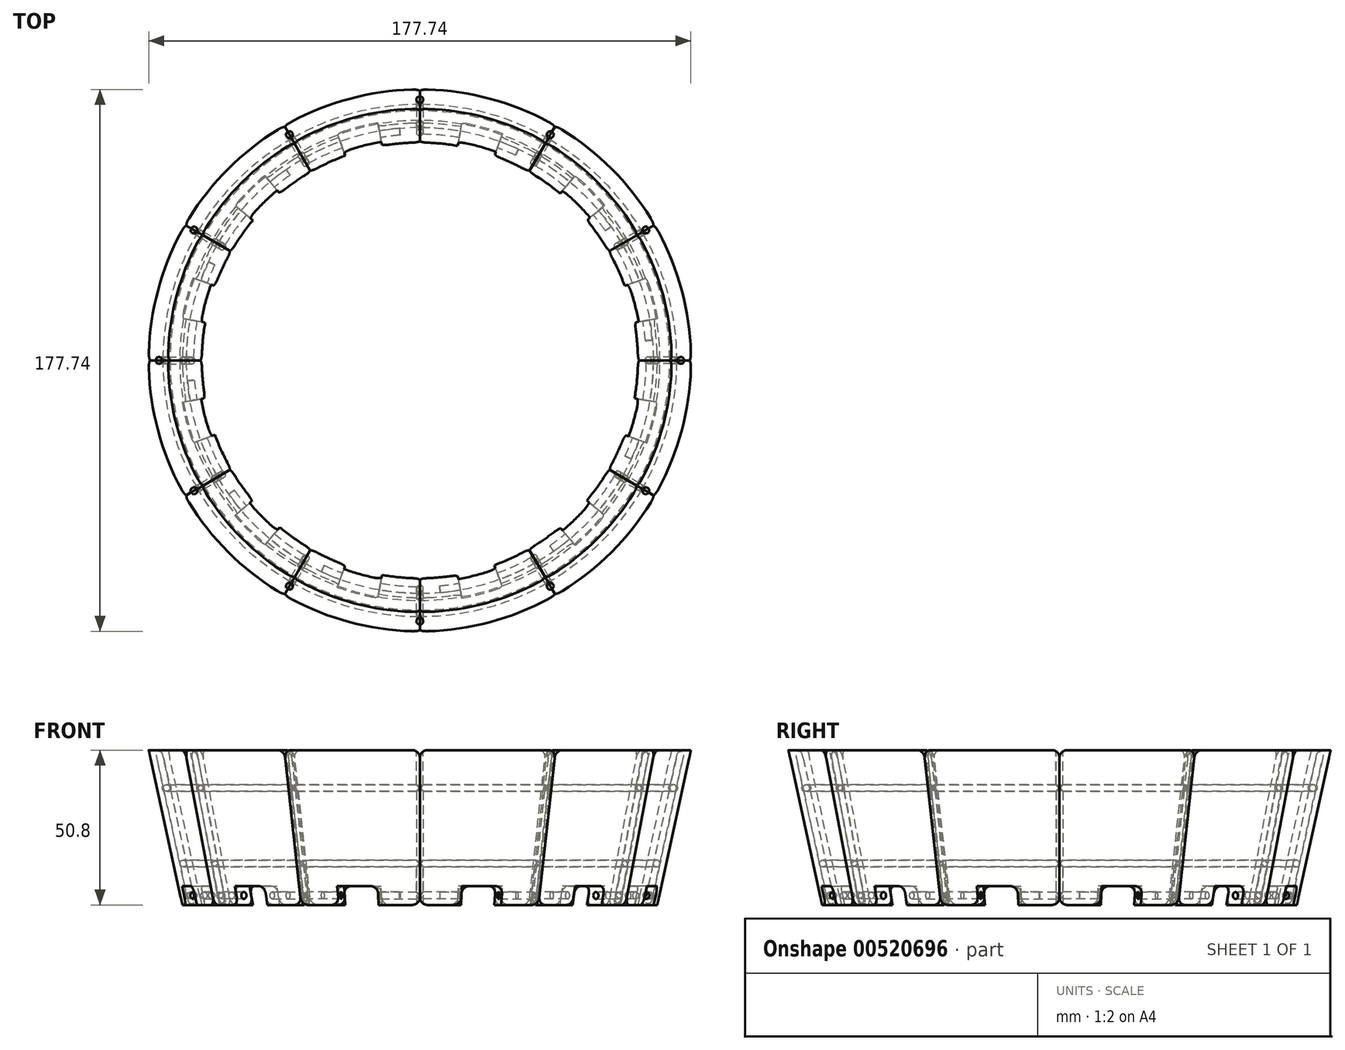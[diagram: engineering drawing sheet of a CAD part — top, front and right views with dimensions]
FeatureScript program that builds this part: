
annotation { "Feature Type Name" : "Feature", "Feature Type Description" : "" }
export const myFeature = defineFeature(function(context is Context, id is Id, definition is map)
    precondition{}
    {
        {
            var Q0;
            Q0=qCreatedBy(makeId("Front.planeOp"),FACE);
            var sketch = newSketch(context, id + "F0", { "sketchPlane" : qUnion([Q0])});
            skLineSegment(sketch, "E0", {"start": v(0, 0) * mm, "end": v(0, 50.8) * mm});
            skLineSegment(sketch, "E1", {"start": v(0, 50.8) * mm, "end": v(88.9, 50.8) * mm});
            skLineSegment(sketch, "E2", {"start": v(0, 0) * mm, "end": v(77.84, 0) * mm});
            skLineSegment(sketch, "E3", {"start": v(77.84, 0) * mm, "end": v(88.9, 50.8) * mm});
            skSolve(sketch);
        }
        {
            var Q0;
            Q0 = qSketchRegion(id + "F0", true);
            var Q1;
            Q1=sQuery(id+"F0.wireOp",EDGE,"E0");
            revolve(context, id + "F1", {"entities" : qUnion([Q0]), "axis" : qUnion([Q1]), "revolveType" : RevolveType.ONE_DIRECTION, "angle" : 30 * degree});
        }
        {
            var Q0;
            Q0=makeQuery(id+"F1.opRevolve","CAP_FACE",FACE,{"disambiguationData":[OSD([sQuery(id+"F0.wireOp",EDGE,"E0"),sQuery(id+"F0.wireOp",EDGE,"E1"),sQuery(id+"F0.wireOp",EDGE,"E2"),sQuery(id+"F0.wireOp",EDGE,"E3")])],"isStart":true});
            var sketch = newSketch(context, id + "F2", { "sketchPlane" : qUnion([Q0])});
            skLineSegment(sketch, "E4", {"start": v(0, 0) * mm, "end": v(0, 50.8) * mm});
            skLineSegment(sketch, "E5", {"start": v(0, 50.8) * mm, "end": v(82.55, 50.8) * mm});
            skLineSegment(sketch, "E6", {"start": v(0, 0) * mm, "end": v(71.49, 0) * mm});
            skLineSegment(sketch, "E7", {"start": v(71.49, 0) * mm, "end": v(82.55, 50.8) * mm});
            skSolve(sketch);
        }
        {
            var Q0;
            Q0 = qSketchRegion(id + "F2", true);
            var Q1;
            Q1=sQuery(id+"F2.wireOp",EDGE,"E4");
            revolve(context, id + "F3", {"operationType" : NewBodyOperationType.REMOVE, "entities" : qUnion([Q0]), "axis" : qUnion([Q1]), "revolveType" : RevolveType.FULL, "oppositeDirection" : true});
        }
        {
            var Q0;
            Q0=makeQuery(id+"F1.opRevolve","CAP_FACE",FACE,{"disambiguationData":[OSD([sQuery(id+"F0.wireOp",EDGE,"E0"),sQuery(id+"F0.wireOp",EDGE,"E1"),sQuery(id+"F0.wireOp",EDGE,"E2"),sQuery(id+"F0.wireOp",EDGE,"E3")])],"isStart":true});
            var sketch = newSketch(context, id + "F4", { "sketchPlane" : qUnion([Q0])});
            skLineSegment(sketch, "E8", {"start": v(0, 0) * mm, "end": v(77.84, 0) * mm, "construction": true});
            skLineSegment(sketch, "E9", {"start": v(77.84, 0) * mm, "end": v(79.19, 6.2) * mm});
            skLineSegment(sketch, "E10", {"start": v(79.19, 6.2) * mm, "end": v(72.84, 6.2) * mm});
            skLineSegment(sketch, "E11", {"start": v(72.84, 6.2) * mm, "end": v(71.49, 0) * mm});
            skLineSegment(sketch, "E12", {"start": v(71.49, 0) * mm, "end": v(77.84, 0) * mm});
            skLineSegment(sketch, "E13", {"start": v(0, 0) * mm, "end": v(0, 20.69) * mm, "construction": true});
            skSolve(sketch);
        }
        {
            var Q0;
            Q0 = qSketchRegion(id + "F4", true);
            var Q1;
            Q1=sQuery(id+"F4.wireOp",EDGE,"E13");
            revolve(context, id + "F5", {"operationType" : NewBodyOperationType.REMOVE, "entities" : qUnion([Q0]), "axis" : qUnion([Q1]), "revolveType" : RevolveType.ONE_DIRECTION, "angle" : 20 * degree});
        }
        {
            var Q0;
            Q0 = qSketchRegion(id + "F4", true);
            var Q1;
            Q1=sQuery(id+"F4.wireOp",EDGE,"E13");
            revolve(context, id + "F6", {"operationType" : NewBodyOperationType.ADD, "entities" : qUnion([Q0]), "axis" : qUnion([Q1]), "revolveType" : RevolveType.ONE_DIRECTION, "angle" : 10 * degree});
        }
        {
            var Q0;
            Q0=makeQuery(id+"F5.boolean.opBoolean","COPY",EDGE,{"derivedFrom":makeQuery(id+"F5.opRevolve","CAP_EDGE",EDGE,{"disambiguationData":[OSD([sQuery(id+"F4.wireOp",EDGE,"E10")])],"isStart":false})});
            var Q1;
            Q1=makeQuery(id+"F6.opRevolve","CAP_EDGE",EDGE,{"disambiguationData":[OSD([sQuery(id+"F4.wireOp",EDGE,"E10")])],"isStart":false});
            var Q2;
            Q2=makeQuery(id+"F6.opRevolve","CAP_EDGE",EDGE,{"disambiguationData":[OSD([sQuery(id+"F4.wireOp",EDGE,"E12")])],"isStart":false});
            var Q3;
            Q3=makeQuery(id+"F6.opRevolve","CAP_EDGE",EDGE,{"disambiguationData":[OSD([sQuery(id+"F4.wireOp",EDGE,"E12")])],"isStart":true});
            var Q4;
            Q4=makeQuery(id+"F5.boolean.opBoolean","COPY",EDGE,{"derivedFrom":makeQuery(id+"F5.opRevolve","CAP_EDGE",EDGE,{"disambiguationData":[OSD([sQuery(id+"F4.wireOp",EDGE,"E12")])],"isStart":false})});
            var Q5;
            Q5=makeQuery(id+"F1.opRevolve","CAP_EDGE",EDGE,{"disambiguationData":[OSD([sQuery(id+"F0.wireOp",EDGE,"E2")])],"isStart":false});
            var Q6;
            Q6=makeQuery(id+"F1.opRevolve","CAP_EDGE",EDGE,{"disambiguationData":[OSD([sQuery(id+"F0.wireOp",EDGE,"E1")])],"isStart":false});
            var Q7;
            Q7=makeQuery(id+"F1.opRevolve","CAP_EDGE",EDGE,{"disambiguationData":[OSD([sQuery(id+"F0.wireOp",EDGE,"E1")])],"isStart":true});
            fillet(context, id + "F7", {"entities" : qUnion([Q0, Q1, Q2, Q3, Q4, Q5, Q6, Q7]), "radius" : 2.54 * mm, "tangentPropagation" : true, "allowEdgeOverflow" : false});
        }
        {
            var Q0;
            Q0=makeQuery(id+"F6.boolean.opBoolean","MERGE",FACE,{"derivedFrom":[makeQuery(id+"F1.opRevolve","CAP_FACE",FACE,{"disambiguationData":[OSD([sQuery(id+"F0.wireOp",EDGE,"E0"),sQuery(id+"F0.wireOp",EDGE,"E1"),sQuery(id+"F0.wireOp",EDGE,"E2"),sQuery(id+"F0.wireOp",EDGE,"E3")])],"isStart":true}),makeQuery(id+"F6.opRevolve","CAP_FACE",FACE,{"disambiguationData":[OSD([sQuery(id+"F4.wireOp",EDGE,"E9"),sQuery(id+"F4.wireOp",EDGE,"E10"),sQuery(id+"F4.wireOp",EDGE,"E11"),sQuery(id+"F4.wireOp",EDGE,"E12")])],"isStart":true})]});
            var sketch = newSketch(context, id + "F8", { "sketchPlane" : qUnion([Q0])});
            skLineSegment(sketch, "E14", {"start": v(0, 0) * mm, "end": v(0, 50.8) * mm, "construction": true});
            skLineSegment(sketch, "E15", {"start": v(0, 50.8) * mm, "end": v(88.9, 50.8) * mm, "construction": true});
            skLineSegment(sketch, "E16", {"start": v(0, 0) * mm, "end": v(77.84, 0) * mm, "construction": true});
            skLineSegment(sketch, "E17", {"start": v(77.84, 0) * mm, "end": v(88.9, 50.8) * mm, "construction": true});
            skLineSegment(sketch, "E18", {"start": v(77.84, 0) * mm, "end": v(78.51, 3.1) * mm, "construction": true});
            skLineSegment(sketch, "E19", {"start": v(78.51, 3.1) * mm, "end": v(75.34, 3.1) * mm, "construction": true});
            skCircle(sketch, "E20", {"center": v(75.34, 3.1) * mm, "radius": 1.11 * mm});
            skLineSegment(sketch, "E21", {"start": v(88.9, 50.8) * mm, "end": v(86.2, 38.4) * mm, "construction": true});
            skLineSegment(sketch, "E22", {"start": v(86.2, 38.4) * mm, "end": v(83.02, 38.4) * mm, "construction": true});
            skCircle(sketch, "E23", {"center": v(83.02, 38.4) * mm, "radius": 1.11 * mm});
            skLineSegment(sketch, "E24", {"start": v(75.34, 3.1) * mm, "end": v(83.02, 38.4) * mm, "construction": true});
            skPoint(sketch, "E25", {"position": v(77.62, 13.57) * mm});
            skCircle(sketch, "E26", {"center": v(77.62, 13.57) * mm, "radius": 1.11 * mm});
            skSolve(sketch);
        }
        {
            var Q0;
            Q0 = qSketchRegion(id + "F8", true);
            var Q1;
            Q1=sQuery(id+"F8.wireOp",EDGE,"E14");
            revolve(context, id + "F9", {"operationType" : NewBodyOperationType.REMOVE, "entities" : qUnion([Q0]), "axis" : qUnion([Q1]), "revolveType" : RevolveType.FULL, "oppositeDirection" : true});
        }
        {
            var Q0;
            {var subQ0=sQuery(id+"F8.wireOp",EDGE,"E20");var subQ1=sQuery(id+"F4.wireOp",EDGE,"E12");var subQ2=makeQuery(id+"F7.opFillet","BLEND_EDGE",EDGE,{"blendedFrom":[makeQuery(id+"F6.opRevolve","CAP_EDGE",EDGE,{"disambiguationData":[OSD([subQ1])],"isStart":true}),makeQuery(id+"F6.boolean.opBoolean","MERGE",FACE,{"derivedFrom":[makeQuery(id+"F1.opRevolve","CAP_FACE",FACE,{"disambiguationData":[OSD([sQuery(id+"F0.wireOp",EDGE,"E0"),sQuery(id+"F0.wireOp",EDGE,"E1"),sQuery(id+"F0.wireOp",EDGE,"E2"),sQuery(id+"F0.wireOp",EDGE,"E3")])],"isStart":true}),makeQuery(id+"F6.opRevolve","CAP_FACE",FACE,{"disambiguationData":[OSD([sQuery(id+"F4.wireOp",EDGE,"E9"),sQuery(id+"F4.wireOp",EDGE,"E10"),sQuery(id+"F4.wireOp",EDGE,"E11"),subQ1])],"isStart":true})]})],"blendedInto":[makeQuery(id+"F6.boolean.opBoolean","MERGE",FACE,{"derivedFrom":[makeQuery(id+"F1.opRevolve","CAP_FACE",FACE,{"disambiguationData":[OSD([sQuery(id+"F0.wireOp",EDGE,"E0"),sQuery(id+"F0.wireOp",EDGE,"E1"),sQuery(id+"F0.wireOp",EDGE,"E2"),sQuery(id+"F0.wireOp",EDGE,"E3")])],"isStart":true}),makeQuery(id+"F6.opRevolve","CAP_FACE",FACE,{"disambiguationData":[OSD([sQuery(id+"F4.wireOp",EDGE,"E9"),sQuery(id+"F4.wireOp",EDGE,"E10"),sQuery(id+"F4.wireOp",EDGE,"E11"),subQ1])],"isStart":true})]})]});var subQ3=makeQuery(id+"F8.imprint","INTERSECT",VERTEX,{"disambiguationData":[OD(0.0)],"derivedFrom":[subQ2,subQ0]});Q0=makeQuery(id+"F8.imprint","IMPRINT",FACE,{"disambiguationData":[TD([[makeQuery(id+"F8.imprint","IMPRINT",EDGE,{"disambiguationData":[TD([[subQ3,1.0]])],"derivedFrom":subQ0}),1.0]])]});}
            var Q1;
            {var subQ0=sQuery(id+"F8.wireOp",EDGE,"E20");var subQ1=sQuery(id+"F4.wireOp",EDGE,"E12");var subQ2=makeQuery(id+"F7.opFillet","BLEND_EDGE",EDGE,{"blendedFrom":[makeQuery(id+"F6.opRevolve","CAP_EDGE",EDGE,{"disambiguationData":[OSD([subQ1])],"isStart":true}),makeQuery(id+"F6.boolean.opBoolean","MERGE",FACE,{"derivedFrom":[makeQuery(id+"F1.opRevolve","CAP_FACE",FACE,{"disambiguationData":[OSD([sQuery(id+"F0.wireOp",EDGE,"E0"),sQuery(id+"F0.wireOp",EDGE,"E1"),sQuery(id+"F0.wireOp",EDGE,"E2"),sQuery(id+"F0.wireOp",EDGE,"E3")])],"isStart":true}),makeQuery(id+"F6.opRevolve","CAP_FACE",FACE,{"disambiguationData":[OSD([sQuery(id+"F4.wireOp",EDGE,"E9"),sQuery(id+"F4.wireOp",EDGE,"E10"),sQuery(id+"F4.wireOp",EDGE,"E11"),subQ1])],"isStart":true})]})],"blendedInto":[makeQuery(id+"F6.boolean.opBoolean","MERGE",FACE,{"derivedFrom":[makeQuery(id+"F1.opRevolve","CAP_FACE",FACE,{"disambiguationData":[OSD([sQuery(id+"F0.wireOp",EDGE,"E0"),sQuery(id+"F0.wireOp",EDGE,"E1"),sQuery(id+"F0.wireOp",EDGE,"E2"),sQuery(id+"F0.wireOp",EDGE,"E3")])],"isStart":true}),makeQuery(id+"F6.opRevolve","CAP_FACE",FACE,{"disambiguationData":[OSD([sQuery(id+"F4.wireOp",EDGE,"E9"),sQuery(id+"F4.wireOp",EDGE,"E10"),sQuery(id+"F4.wireOp",EDGE,"E11"),subQ1])],"isStart":true})]})]});var subQ3=makeQuery(id+"F8.imprint","INTERSECT",VERTEX,{"disambiguationData":[OD(0.0)],"derivedFrom":[subQ2,subQ0]});Q1=makeQuery(id+"F8.imprint","IMPRINT",FACE,{"disambiguationData":[TD([[makeQuery(id+"F8.imprint","IMPRINT",EDGE,{"disambiguationData":[TD([[subQ3,-1.0]])],"derivedFrom":subQ0}),1.0]])]});}
            var Q2;
            Q2=sQuery(id+"F8.wireOp",EDGE,"E14");
            revolve(context, id + "F10", {"operationType" : NewBodyOperationType.ADD, "entities" : qUnion([Q0, Q1]), "axis" : qUnion([Q2]), "revolveType" : RevolveType.ONE_DIRECTION, "angle" : 5 * degree});
        }
        {
            var Q0;
            Q0=makeQuery(id+"F9.boolean.opBoolean","INTERSECT",EDGE,{"derivedFrom":[makeQuery(id+"F6.boolean.opBoolean","MERGE",FACE,{"derivedFrom":[makeQuery(id+"F1.opRevolve","CAP_FACE",FACE,{"disambiguationData":[OSD([sQuery(id+"F0.wireOp",EDGE,"E0"),sQuery(id+"F0.wireOp",EDGE,"E1"),sQuery(id+"F0.wireOp",EDGE,"E2"),sQuery(id+"F0.wireOp",EDGE,"E3")])],"isStart":true}),makeQuery(id+"F6.opRevolve","CAP_FACE",FACE,{"disambiguationData":[OSD([sQuery(id+"F4.wireOp",EDGE,"E9"),sQuery(id+"F4.wireOp",EDGE,"E10"),sQuery(id+"F4.wireOp",EDGE,"E11"),sQuery(id+"F4.wireOp",EDGE,"E12")])],"isStart":true})]}),makeQuery(id+"F9.opRevolve","SWEPT_FACE",FACE,{"disambiguationData":[OSD([sQuery(id+"F8.wireOp",EDGE,"E23")])]})]});
            var Q1;
            Q1=makeQuery(id+"F9.boolean.opBoolean","INTERSECT",EDGE,{"derivedFrom":[makeQuery(id+"F6.boolean.opBoolean","MERGE",FACE,{"derivedFrom":[makeQuery(id+"F1.opRevolve","CAP_FACE",FACE,{"disambiguationData":[OSD([sQuery(id+"F0.wireOp",EDGE,"E0"),sQuery(id+"F0.wireOp",EDGE,"E1"),sQuery(id+"F0.wireOp",EDGE,"E2"),sQuery(id+"F0.wireOp",EDGE,"E3")])],"isStart":true}),makeQuery(id+"F6.opRevolve","CAP_FACE",FACE,{"disambiguationData":[OSD([sQuery(id+"F4.wireOp",EDGE,"E9"),sQuery(id+"F4.wireOp",EDGE,"E10"),sQuery(id+"F4.wireOp",EDGE,"E11"),sQuery(id+"F4.wireOp",EDGE,"E12")])],"isStart":true})]}),makeQuery(id+"F9.opRevolve","SWEPT_FACE",FACE,{"disambiguationData":[OSD([sQuery(id+"F8.wireOp",EDGE,"E20")])]})]});
            var Q2;
            Q2=makeQuery(id+"F9.boolean.opBoolean","INTERSECT",EDGE,{"derivedFrom":[makeQuery(id+"F1.opRevolve","CAP_FACE",FACE,{"disambiguationData":[OSD([sQuery(id+"F0.wireOp",EDGE,"E0"),sQuery(id+"F0.wireOp",EDGE,"E1"),sQuery(id+"F0.wireOp",EDGE,"E2"),sQuery(id+"F0.wireOp",EDGE,"E3")])],"isStart":false}),makeQuery(id+"F9.opRevolve","SWEPT_FACE",FACE,{"disambiguationData":[OSD([sQuery(id+"F8.wireOp",EDGE,"E23")])]})]});
            var Q3;
            Q3=makeQuery(id+"F9.boolean.opBoolean","INTERSECT",EDGE,{"derivedFrom":[makeQuery(id+"F1.opRevolve","CAP_FACE",FACE,{"disambiguationData":[OSD([sQuery(id+"F0.wireOp",EDGE,"E0"),sQuery(id+"F0.wireOp",EDGE,"E1"),sQuery(id+"F0.wireOp",EDGE,"E2"),sQuery(id+"F0.wireOp",EDGE,"E3")])],"isStart":false}),makeQuery(id+"F9.opRevolve","SWEPT_FACE",FACE,{"disambiguationData":[OSD([sQuery(id+"F8.wireOp",EDGE,"E20")])]})]});
            fillet(context, id + "F11", {"entities" : qUnion([Q0, Q1, Q2, Q3]), "radius" : 0.32 * mm, "tangentPropagation" : true, "allowEdgeOverflow" : false});
        }
        {
            var Q0;
            Q0=qCreatedBy(makeId("Front.planeOp"),FACE);
            var sketch = newSketch(context, id + "F12", { "sketchPlane" : qUnion([Q0])});
            skLineSegment(sketch, "E27", {"start": v(0, 0) * mm, "end": v(0, 41.72) * mm, "construction": true});
            skSolve(sketch);
        }
        {
            var Q0;
            Q0=makeQuery(id+"F6.opRevolve","SWEPT_FACE",FACE,{"disambiguationData":[OSD([sQuery(id+"F4.wireOp",EDGE,"E12")])]});
            var sketch = newSketch(context, id + "F13", { "sketchPlane" : qUnion([Q0])});
            skLineSegment(sketch, "E28", {"start": v(0, 0) * mm, "end": v(77.84, 0) * mm, "construction": true});
            skPoint(sketch, "E29", {"position": v(74.66, 0) * mm});
            skCircle(sketch, "E30", {"center": v(74.66, 0) * mm, "radius": 1.11 * mm});
            skLineSegment(sketch, "E31", {"start": v(0, 0) * mm, "end": v(67.4, -38.93) * mm, "construction": true});
            skPoint(sketch, "E32", {"position": v(64.65, -37.35) * mm});
            skCircle(sketch, "E33", {"center": v(64.65, -37.35) * mm, "radius": 1.11 * mm});
            skSolve(sketch);
        }
        {
            var Q0;
            Q0=makeQuery(id+"F1.opRevolve","SWEPT_FACE",FACE,{"disambiguationData":[OSD([sQuery(id+"F0.wireOp",EDGE,"E1")])]});
            var sketch = newSketch(context, id + "F14", { "sketchPlane" : qUnion([Q0])});
            skLineSegment(sketch, "E34", {"start": v(0, 0) * mm, "end": v(88.9, 0) * mm, "construction": true});
            skPoint(sketch, "E35", {"position": v(85.73, 0) * mm});
            skCircle(sketch, "E36", {"center": v(85.73, 0) * mm, "radius": 1.11 * mm});
            skLineSegment(sketch, "E37", {"start": v(0, 0) * mm, "end": v(76.99, 44.45) * mm, "construction": true});
            skPoint(sketch, "E38", {"position": v(74.24, 42.86) * mm});
            skCircle(sketch, "E39", {"center": v(74.24, 42.86) * mm, "radius": 1.11 * mm});
            skSolve(sketch);
        }
        {
            var Q1;
            Q1=makeQuery(id+"F14.imprint","IMPRINT",FACE,{"disambiguationData":[TD([[makeQuery(id+"F14.imprint","IMPRINT",EDGE,{"derivedFrom":sQuery(id+"F14.wireOp",EDGE,"E36")}),1.0]])]});
            var Q2;
            Q2=makeQuery(id+"F13.imprint","IMPRINT",FACE,{"disambiguationData":[TD([[makeQuery(id+"F13.imprint","IMPRINT",EDGE,{"derivedFrom":sQuery(id+"F13.wireOp",EDGE,"E30")}),1.0]])]});
            loft(context, id + "F15", {"operationType" : NewBodyOperationType.REMOVE, "sheetProfilesArray" : [{ "sheetProfileEntities" : qUnion([Q1]) }, { "sheetProfileEntities" : qUnion([Q2]) }]});
        }
        {
            var Q1;
            Q1=makeQuery(id+"F14.imprint","IMPRINT",FACE,{"disambiguationData":[TD([[makeQuery(id+"F14.imprint","IMPRINT",EDGE,{"derivedFrom":sQuery(id+"F14.wireOp",EDGE,"E39")}),1.0]])]});
            var Q2;
            Q2=makeQuery(id+"F13.imprint","IMPRINT",FACE,{"disambiguationData":[TD([[makeQuery(id+"F13.imprint","IMPRINT",EDGE,{"derivedFrom":sQuery(id+"F13.wireOp",EDGE,"E33")}),1.0]])]});
            loft(context, id + "F16", {"operationType" : NewBodyOperationType.REMOVE, "sheetProfilesArray" : [{ "sheetProfileEntities" : qUnion([Q1]) }, { "sheetProfileEntities" : qUnion([Q2]) }]});
        }
        {
            var Q0;
            Q0=makeQuery(id+"F1.opRevolve","SWEPT_BODY",BODY,{"disambiguationData":[OSD([sQuery(id+"F0.wireOp",EDGE,"E0"),sQuery(id+"F0.wireOp",EDGE,"E1"),sQuery(id+"F0.wireOp",EDGE,"E2"),sQuery(id+"F0.wireOp",EDGE,"E3")])]});
            var Q1;
            Q1=sQuery(id+"F12.wireOp",EDGE,"E27");
            circularPattern(context, id + "F17", {"entities" : qUnion([Q0]), "axis" : qUnion([Q1]), "angle" : 360 * degree, "instanceCount" : 12, "equalSpace" : true});
        }
    });
